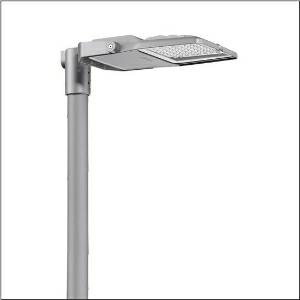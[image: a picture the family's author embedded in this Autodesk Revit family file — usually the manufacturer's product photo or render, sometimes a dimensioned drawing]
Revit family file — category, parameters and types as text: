
# Revit family: floodlight_fl_21_mini___pl33t_5xa7776d2f3a_276e
name_source: partatom
category: Lighting Fixtures
units: mm (PartAtom-declared; Revit-internal decimal feet)

## family parameters
Cut with Voids When Loaded = No
Host = Face
Light Source = No
Part Type = Normal
Room Calculation Point = No
Round Connector Dimension = Use Diameter
Shared = No

## types (1)
- --- (1 x LED, 17630 lm, 142.9 W, 3000K)
    Apparent Load = 143 VA
    CIE Flux Codes = 26 75 99 100 100
    Color Rendering = 70
    Color Temperature = 3000K
    Default Elevation = 1800 mm
    Description = Floodlight FL 21 mini, floodlight, primary light control with lens, of PMMA, primary optical cover: protective disc, of toughened safety glass, transparent, light distribution: PL33T, light emission: direct distribution, installation type: surface-mounted, LED, High Power LED, rated luminous flux: 17.630lm, luminous efficacy: 123lm/W, light colour: 730, colour temperature: 3000K, control gear: Smart Interface (Zhaga), control: flexible luminous flux parameterisation, time-dependent luminous flux control, constant luminous flux control, overheat protection, pre-setting: logarithmic dimming characteristic, with terminal, 6-pole, mains connection: 220..240V, AC, 50/60Hz, start of lifetime: 143W, end of service life: 151W, reduction: 63W, luminaire housing, of diecast aluminium, powder-coated, Siteco® metallic grey (DB 702S), corrosivity category C5 mid according to DIN EN ISO 12944, suitable for swimming pools, chlorine-resistant, sealing non-destructively replaceable, please order mast flange separately, mast bracket, of steel, galvanised, powder-coated, Siteco® metallic grey (DB 702S), Smart Interface below and above, protection rating (complete): IP66, insulation class (complete): insulation class II (safety insulation), certification: CE, ENEC, VDE, protection symbol: D, impact resistance: IK08, permissible operating ambient temperature: -40..+40°C, permissible operating ambient temperature for outdoor applications: -40..+50°C, standard: DIN EN 12944, LABS conformity tested according to VDMA 24364:2018-05, packaging unit: 1 piece

Light Distribution: PL33T
    Height = 70 mm
    Lamp = 1 x LED
    Lamp Light Flux = 17630 lm
    Lamp Power = 142.9 W
    Lamp count = 1
    Length = 485 mm
    Luminous efficacy = 123 lm/W
    Manufacturer = Siteco
    ModVariant = No
    Model = 5XA7776D2F3A
    Number of Poles = 1
    OnlyDefault = Yes
    Power Factor = 1
    Product Name = Floodlight FL 21 mini | PL33T
    Product group = floodlight | pylon annexe
    ProductGroupID = 6201
    Protection Class = Protection class II
    Protection Degree = IP 66
    RLX_Detail_Level = 1
    RLX_Emergency_Light_Flux = 0 lm
    RLX_Emergency_Type = 0
    RLX_Emergency_Type_DB = No
    RlxData = <blob elided: 101333 chars, md5=dc721424>
    Socket = socket
    Standby Power = 0 W
    System Light Flux = 17630 lm
    System Power = 143 W
    Type Comments = factory setting: luminous flux: 100 % | dim-lin: 254 | 730 mA
    Type Image = l_1007125.jpg
    URL = http://relux.com
    VarID = @adj_169767
    Voltage = 0 V
    Weight = 0.00 kg
    Width = 337 mm

## geometry (parser evidence)
native form markers: Blend x4, Sweep x13
no freeform markers — native parametric forms only
